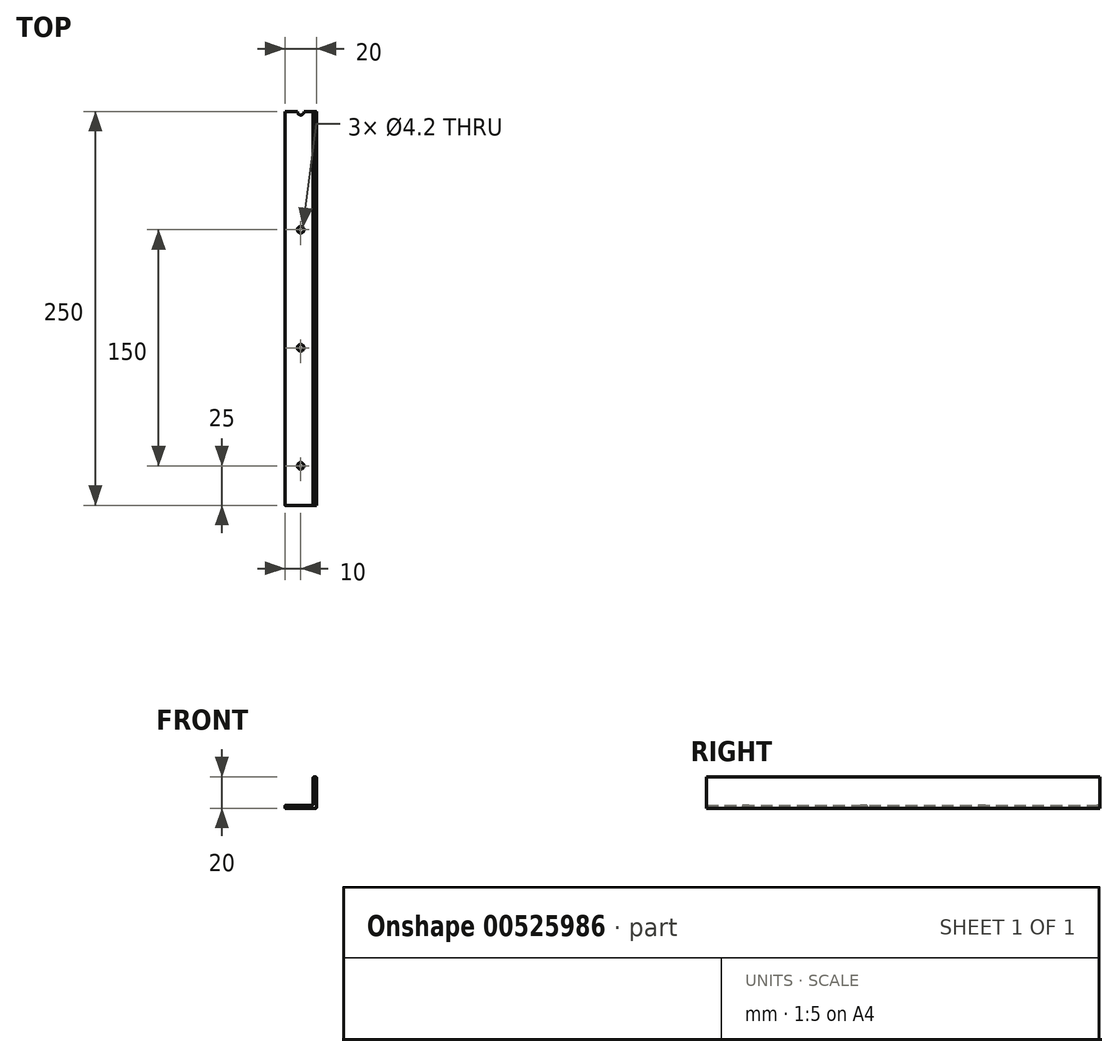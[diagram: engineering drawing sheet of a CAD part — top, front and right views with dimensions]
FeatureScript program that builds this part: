
annotation { "Feature Type Name" : "Feature", "Feature Type Description" : "" }
export const myFeature = defineFeature(function(context is Context, id is Id, definition is map)
    precondition{}
    {
        {
            var Q0;
            Q0=qCreatedBy(makeId("Front.planeOp"),FACE);
            var sketch = newSketch(context, id + "F0", { "sketchPlane" : qUnion([Q0])});
            skLineSegment(sketch, "E0", {"start": v(0, 0.5) * mm, "end": v(0, 19.5) * mm});
            skLineSegment(sketch, "E1", {"start": v(-0.5, 20) * mm, "end": v(-1.5, 20) * mm});
            skLineSegment(sketch, "E2", {"start": v(-2, 19.5) * mm, "end": v(-2, 2.5) * mm});
            skLineSegment(sketch, "E3", {"start": v(-2.5, 2) * mm, "end": v(-19.5, 2) * mm});
            skLineSegment(sketch, "E4", {"start": v(-20, 1.5) * mm, "end": v(-20, 0.5) * mm});
            skLineSegment(sketch, "E5", {"start": v(-19.5, 0) * mm, "end": v(-0.5, 0) * mm});
            skPoint(sketch, "E6.visualSharp", {"position": v(-2, 20) * mm});
            skArc(sketch, "E6.filletArc", {"start": v(-1.5, 20) * mm, "mid": v(-1.85, 19.85) * mm, "end": v(-2, 19.5) * mm});
            skPoint(sketch, "E7.visualSharp", {"position": v(0, 20) * mm});
            skArc(sketch, "E7.filletArc", {"start": v(0, 19.5) * mm, "mid": v(-0.15, 19.85) * mm, "end": v(-0.5, 20) * mm});
            skPoint(sketch, "E8.visualSharp", {"position": v(0, 0) * mm});
            skArc(sketch, "E8.filletArc", {"start": v(-0.5, 0) * mm, "mid": v(-0.15, 0.15) * mm, "end": v(0, 0.5) * mm});
            skPoint(sketch, "E9.visualSharp", {"position": v(-2, 2) * mm});
            skArc(sketch, "E9.filletArc", {"start": v(-2.5, 2) * mm, "mid": v(-2.15, 2.15) * mm, "end": v(-2, 2.5) * mm});
            skPoint(sketch, "E10.visualSharp", {"position": v(-20, 0) * mm});
            skArc(sketch, "E10.filletArc", {"start": v(-20, 0.5) * mm, "mid": v(-19.85, 0.15) * mm, "end": v(-19.5, 0) * mm});
            skPoint(sketch, "E11.visualSharp", {"position": v(-20, 2) * mm});
            skArc(sketch, "E11.filletArc", {"start": v(-19.5, 2) * mm, "mid": v(-19.85, 1.85) * mm, "end": v(-20, 1.5) * mm});
            skSolve(sketch);
        }
        {
            var Q0;
            Q0=makeQuery(id+"F0.imprint","IMPRINT",FACE,{"disambiguationData":[TD([[makeQuery(id+"F0.imprint","IMPRINT",EDGE,{"derivedFrom":sQuery(id+"F0.wireOp",EDGE,"E0")}),1.0]])]});
            var Q1;
            Q1=sQuery(id+"F0.wireOp",EDGE,"E2");
            var Q2;
            Q2=sQuery(id+"F0.wireOp",EDGE,"E1");
            var Q3;
            Q3=sQuery(id+"F0.wireOp",EDGE,"E0");
            var Q4;
            Q4=sQuery(id+"F0.wireOp",EDGE,"E3");
            var Q5;
            Q5=sQuery(id+"F0.wireOp",EDGE,"E4");
            var Q6;
            Q6=sQuery(id+"F0.wireOp",EDGE,"E5");
            var Q7;
            Q7=sQuery(id+"F0.wireOp",EDGE,"E9.filletArc");
            var Q8;
            Q8=sQuery(id+"F0.wireOp",EDGE,"E11.filletArc");
            var Q9;
            Q9=sQuery(id+"F0.wireOp",EDGE,"E10.filletArc");
            var Q10;
            Q10=sQuery(id+"F0.wireOp",EDGE,"E8.filletArc");
            var Q11;
            Q11=sQuery(id+"F0.wireOp",EDGE,"E6.filletArc");
            var Q12;
            Q12=sQuery(id+"F0.wireOp",EDGE,"E7.filletArc");
            extrude(context, id + "F1", {"entities" : qUnion([Q0]), "surfaceEntities" : qUnion([Q1, Q2, Q3, Q4, Q5, Q6, Q7, Q8, Q9, Q10, Q11, Q12]), "depth" : 250 * mm, "offsetDistance" : 25 * mm});
        }
        {
            var Q0;
            Q0=makeQuery(id+"F1.opExtrude","SWEPT_FACE",FACE,{"disambiguationData":[OSD([sQuery(id+"F0.wireOp",EDGE,"E5")])]});
            var sketch = newSketch(context, id + "F2", { "sketchPlane" : qUnion([Q0])});
            skLineSegment(sketch, "E12", {"start": v(-10, 0) * mm, "end": v(-10, 250) * mm, "construction": true});
            skCircle(sketch, "E13", {"center": v(-10, 225) * mm, "radius": 2.1 * mm});
            skCircle(sketch, "E14.0.1.0", {"center": v(-10, 150) * mm, "radius": 2.1 * mm});
            skLineSegment(sketch, "E14.0.1.1", {"start": v(-10, -75) * mm, "end": v(-10, 175) * mm, "construction": true});
            skCircle(sketch, "E14.0.2.0", {"center": v(-10, 75) * mm, "radius": 2.1 * mm});
            skLineSegment(sketch, "E14.0.2.1", {"start": v(-10, -150) * mm, "end": v(-10, 100) * mm, "construction": true});
            skCircle(sketch, "E14.0.3.0", {"center": v(-10, 0) * mm, "radius": 2.1 * mm});
            skLineSegment(sketch, "E14.0.3.1", {"start": v(-10, -225) * mm, "end": v(-10, 25) * mm, "construction": true});
            skCircle(sketch, "E14.0.4.0", {"center": v(-10, -75) * mm, "radius": 2.1 * mm});
            skLineSegment(sketch, "E14.0.4.1", {"start": v(-10, -300) * mm, "end": v(-10, -50) * mm, "construction": true});
            skLineSegment(sketch, "E14.direction1", {"start": v(-10, 275) * mm, "end": v(15, 275) * mm, "construction": true});
            skLineSegment(sketch, "E14.direction2", {"start": v(-10, 275) * mm, "end": v(-10, 200) * mm, "construction": true});
            skSolve(sketch);
        }
        {
            var Q0;
            Q0 = qSketchRegion(id + "F2", true);
            extrude(context, id + "F3", {"entities" : qUnion([Q0]), "operationType" : NewBodyOperationType.REMOVE, "oppositeDirection" : true, "depth" : 25 * mm, "offsetDistance" : 25 * mm});
        }
    });
